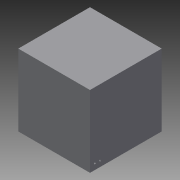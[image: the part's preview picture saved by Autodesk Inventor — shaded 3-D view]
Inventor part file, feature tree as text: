
AUTODESK INVENTOR PART (.ipt)
format: ipt  version: 2014 (Build 180170000, 170)  size: 197,120 bytes
history: native  units: mm
features: other x48, extrude x22, sketch x22
ambient origin geometry x8: Origin, YZ Plane, XZ Plane, XY Plane, X Axis, Y Axis, Z Axis, Center Point
bodies: 实体1 (feature_tree)
feature tree (92):
  extrude  "拉伸1"  Depth=30.2mm
  other  "UCS1"
  other  "UCS2"
  other  "UCS3"
  other  "UCS4"
  other  "UCS5"
  other  "UCS6"
  extrude  "拉伸2"  Depth=70.0mm
  extrude  "拉伸3"  Depth=0.79mm
  extrude  "拉伸5"  Depth=22.22mm
  extrude  "拉伸6"  Depth=14.28mm
  extrude  "拉伸7"  Depth=16.5mm TaperAngle=0.0deg
  extrude  "拉伸8"  Depth=38.5mm TaperAngle=0.0deg
  extrude  "拉伸9"  Depth=17.5mm
  extrude  "拉伸10"  Depth=47.63mm
  extrude  "拉伸11"  Depth=63.5mm TaperAngle=0.0deg
  extrude  "拉伸12"  Depth=30.2mm
  extrude  "拉伸13"  Depth=140.0mm
  extrude  "拉伸14"  Depth=0.79mm
  extrude  "拉伸15"  Depth=2.74mm
  extrude  "拉伸16"  Depth=12.7mm TaperAngle=0.0deg
  extrude  "拉伸17"  Depth=12.7mm TaperAngle=0.0deg
  extrude  "拉伸18"  Depth=12.7mm
  extrude  "拉伸19"  Depth=12.7mm
  extrude  "拉伸20"  Depth=12.7mm TaperAngle=0.0deg
  extrude  "拉伸21"  Depth=12.7mm
  extrude  "拉伸22"  Depth=12.7mm
  extrude  "拉伸23"  Depth=12.7mm TaperAngle=0.0deg
  sketch  "草图1"  dims[d0=1000.0mm d1=0.0mm]
  sketch  "草图2"  dims[d2=0.0mm d3=0.0mm d4=0.0mm d5=0.0mm d6=0.0mm d7=0.0mm]
  sketch  "草图3"  dims[d8=0.0mm d9=0.0mm d10=0.0mm d11=0.0mm d12=0.0mm d13=0.0mm]
  sketch  "草图6"  dims[d14=0.0mm d15=0.0mm d16=0.0mm d17=0.0mm d18=0.0mm d19=0.0mm]
  sketch  "草图7"  dims[d20=0.0mm d21=0.0mm d22=0.0mm d23=0.0mm d24=0.0mm d25=0.0mm]
  sketch  "草图8"  dims[d26=0.0mm d27=0.0mm d28=0.0mm d29=0.0mm d30=0.0mm d31=0.0mm]
  sketch  "草图9"  dims[d32=0.0mm d33=0.0mm d34=0.0mm d35=0.0mm d36=0.0mm d37=0.0mm d38=30.2mm]
  sketch  "草图10"  dims[d39=80.0mm d40=70.0mm]
  sketch  "草图11"  dims[d41=0.79mm d42=0.0mm d43=24.0mm]
  sketch  "草图12"  dims[d44=2.74mm d45=-2.617994mm d49=22.22mm]
  sketch  "草图13"  dims[d50=14.28mm d51=0.0mm d52=14.28mm d53=-7.853982mm]
  sketch  "草图14"  dims[d54=20.63mm d55=16.5mm d56=0.0mm]
  sketch  "草图16"  dims[d57=19.08mm d58=38.5mm d59=0.0mm]
  sketch  "草图17"  dims[d60=38.5mm d61=-5.235988mm d62=17.5mm]
  sketch  "草图18"  dims[d63=47.63mm d64=0.0mm d65=47.63mm d66=-10.471976mm]
  sketch  "草图19"  dims[d67=15.0mm d68=63.5mm d69=0.0mm]
  sketch  "草图20"  dims[d70=63.5mm d71=-10.297443mm d75=30.2mm]
  sketch  "草图21"  dims[d76=80.0mm d77=140.0mm]
  sketch  "草图22"  dims[d78=0.79mm d79=0.0mm d80=20.7mm]
  sketch  "草图23"  dims[d81=2.74mm d82=-2.617994mm d83=2.74mm d84=-7.853982mm]
  sketch  "草图24"  dims[d85=19.05mm d86=12.7mm d87=0.0mm]
  sketch  "草图25"  dims[d88=17.48mm d89=19.05mm d90=0.0mm d91=19.05mm d92=-10.471976mm d93=12.7mm d94=29.3mm d95=0.0mm d96=29.3mm d97=-10.471976mm d98=11.0mm d99=38.1mm d100=0.0mm d101=38.1mm d102=-10.297443mm]
  other  "UCS1: YZ 平面"
  other  "UCS1: XZ 平面"
  other  "UCS1: XY 平面"
  other  "UCS1: X 轴"
  other  "UCS1: Y 轴"
  other  "UCS1: Z 轴"
  other  "UCS1: 原点"
  other  "UCS2: YZ 平面"
  other  "UCS2: XZ 平面"
  other  "UCS2: XY 平面"
  other  "UCS2: X 轴"
  other  "UCS2: Y 轴"
  other  "UCS2: Z 轴"
  other  "UCS2: 原点"
  other  "UCS3: YZ 平面"
  other  "UCS3: XZ 平面"
  other  "UCS3: XY 平面"
  other  "UCS3: X 轴"
  other  "UCS3: Y 轴"
  other  "UCS3: Z 轴"
  other  "UCS3: 原点"
  other  "UCS4: YZ 平面"
  other  "UCS4: XZ 平面"
  other  "UCS4: XY 平面"
  other  "UCS4: X 轴"
  other  "UCS4: Y 轴"
  other  "UCS4: Z 轴"
  other  "UCS4: 原点"
  other  "UCS5: YZ 平面"
  other  "UCS5: XZ 平面"
  other  "UCS5: XY 平面"
  other  "UCS5: X 轴"
  other  "UCS5: Y 轴"
  other  "UCS5: Z 轴"
  other  "UCS5: 原点"
  other  "UCS6: YZ 平面"
  other  "UCS6: XZ 平面"
  other  "UCS6: XY 平面"
  other  "UCS6: X 轴"
  other  "UCS6: Y 轴"
  other  "UCS6: Z 轴"
  other  "UCS6: 原点"
